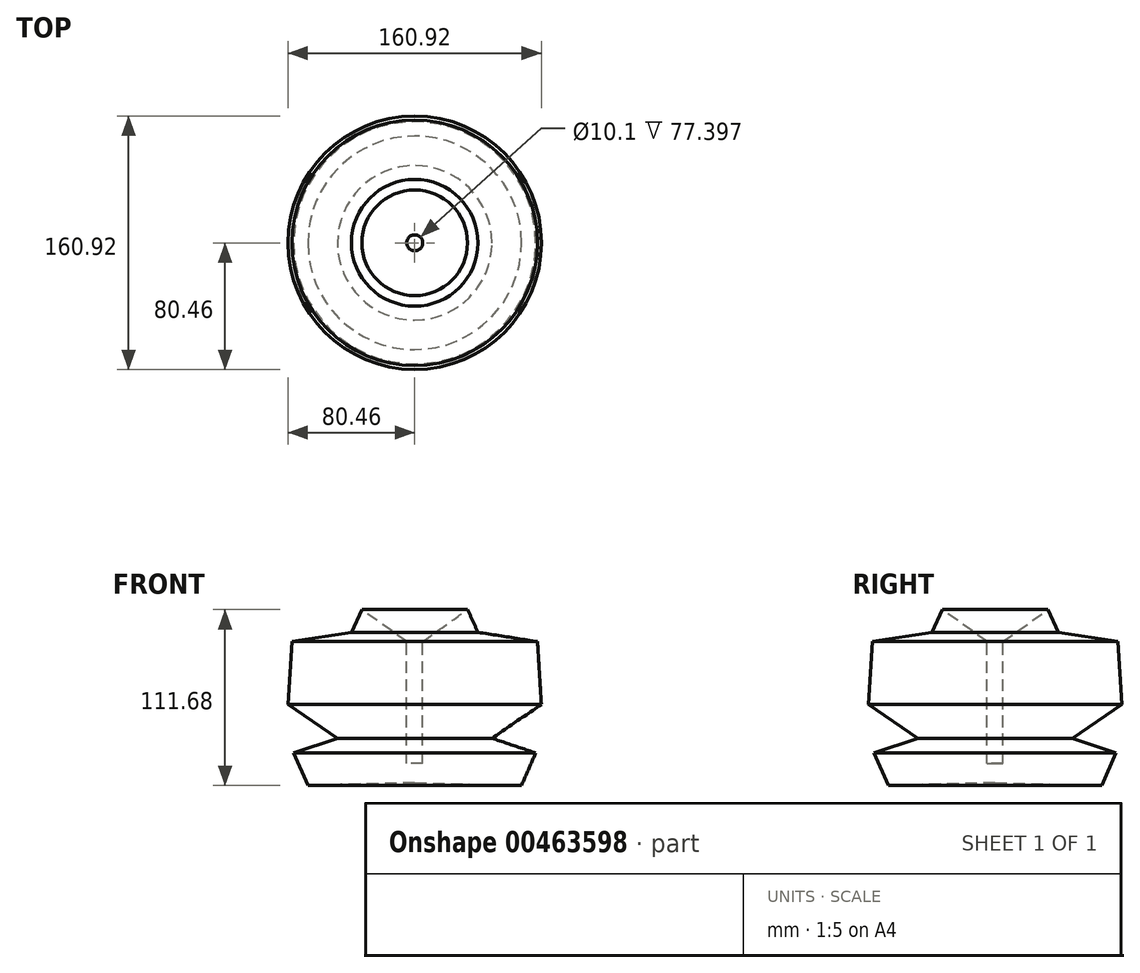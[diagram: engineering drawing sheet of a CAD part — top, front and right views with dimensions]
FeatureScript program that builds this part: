
annotation { "Feature Type Name" : "Feature", "Feature Type Description" : "" }
export const myFeature = defineFeature(function(context is Context, id is Id, definition is map)
    precondition{}
    {
        {
            var Q0;
            Q0=qCreatedBy(makeId("Right.planeOp"),FACE);
            var sketch = newSketch(context, id + "F0", { "sketchPlane" : qUnion([Q0])});
            skLineSegment(sketch, "E0", {"start": v(5.05, 43.93) * mm, "end": v(5.05, -33.47) * mm});
            skLineSegment(sketch, "E1", {"start": v(5.05, -33.47) * mm, "end": v(0, -33.47) * mm});
            skLineSegment(sketch, "E2", {"start": v(0, -33.47) * mm, "end": v(0, -45.73) * mm});
            skLineSegment(sketch, "E3", {"start": v(0, -45.73) * mm, "end": v(67.84, -47.36) * mm});
            skLineSegment(sketch, "E4", {"start": v(67.84, -47.36) * mm, "end": v(76.86, -26.8) * mm});
            skLineSegment(sketch, "E5", {"start": v(76.86, -26.8) * mm, "end": v(49.07, -17.4) * mm});
            skLineSegment(sketch, "E6", {"start": v(49.07, -17.4) * mm, "end": v(80.46, 4.06) * mm});
            skLineSegment(sketch, "E7", {"start": v(80.46, 4.06) * mm, "end": v(77.94, 43.93) * mm});
            skLineSegment(sketch, "E8", {"start": v(77.94, 43.93) * mm, "end": v(40.23, 49.88) * mm});
            skLineSegment(sketch, "E9", {"start": v(40.23, 49.88) * mm, "end": v(33.56, 64.32) * mm});
            skLineSegment(sketch, "E10", {"start": v(33.56, 64.32) * mm, "end": v(5.05, 43.93) * mm});
            skSolve(sketch);
        }
        {
            var Q0;
            Q0 = qSketchRegion(id + "F0", true);
            var Q1;
            Q1=sQuery(id+"F0.wireOp",EDGE,"E2");
            revolve(context, id + "F1", {"entities" : qUnion([Q0]), "axis" : qUnion([Q1]), "revolveType" : RevolveType.FULL});
        }
    });
